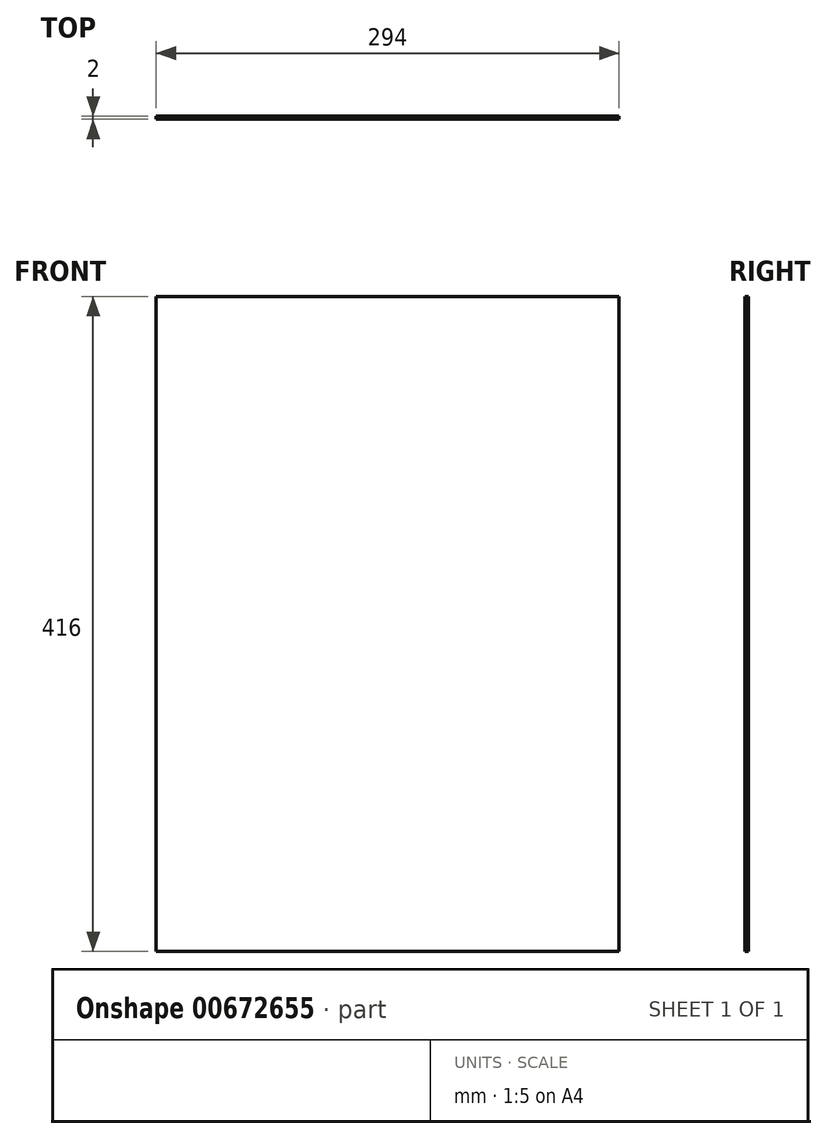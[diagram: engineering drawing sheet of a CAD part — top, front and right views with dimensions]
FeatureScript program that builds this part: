
annotation { "Feature Type Name" : "Feature", "Feature Type Description" : "" }
export const myFeature = defineFeature(function(context is Context, id is Id, definition is map)
    precondition{}
    {
        {
            var Q0;
            Q0=qCreatedBy(makeId("Front.planeOp"),FACE);
            var sketch = newSketch(context, id + "F0", { "sketchPlane" : qUnion([Q0])});
            skLineSegment(sketch, "E0.bottom", {"start": v(0, 0) * mm, "end": v(294, 0) * mm});
            skLineSegment(sketch, "E0.top", {"start": v(0, 416) * mm, "end": v(294, 416) * mm});
            skLineSegment(sketch, "E0.left", {"start": v(0, 0) * mm, "end": v(0, 416) * mm});
            skLineSegment(sketch, "E0.right", {"start": v(294, 0) * mm, "end": v(294, 416) * mm});
            skSolve(sketch);
        }
        {
            var Q0;
            Q0 = qSketchRegion(id + "F0", true);
            extrude(context, id + "F1", {"entities" : qUnion([Q0]), "depth" : 2 * mm, "offsetDistance" : 25 * mm});
        }
    });
